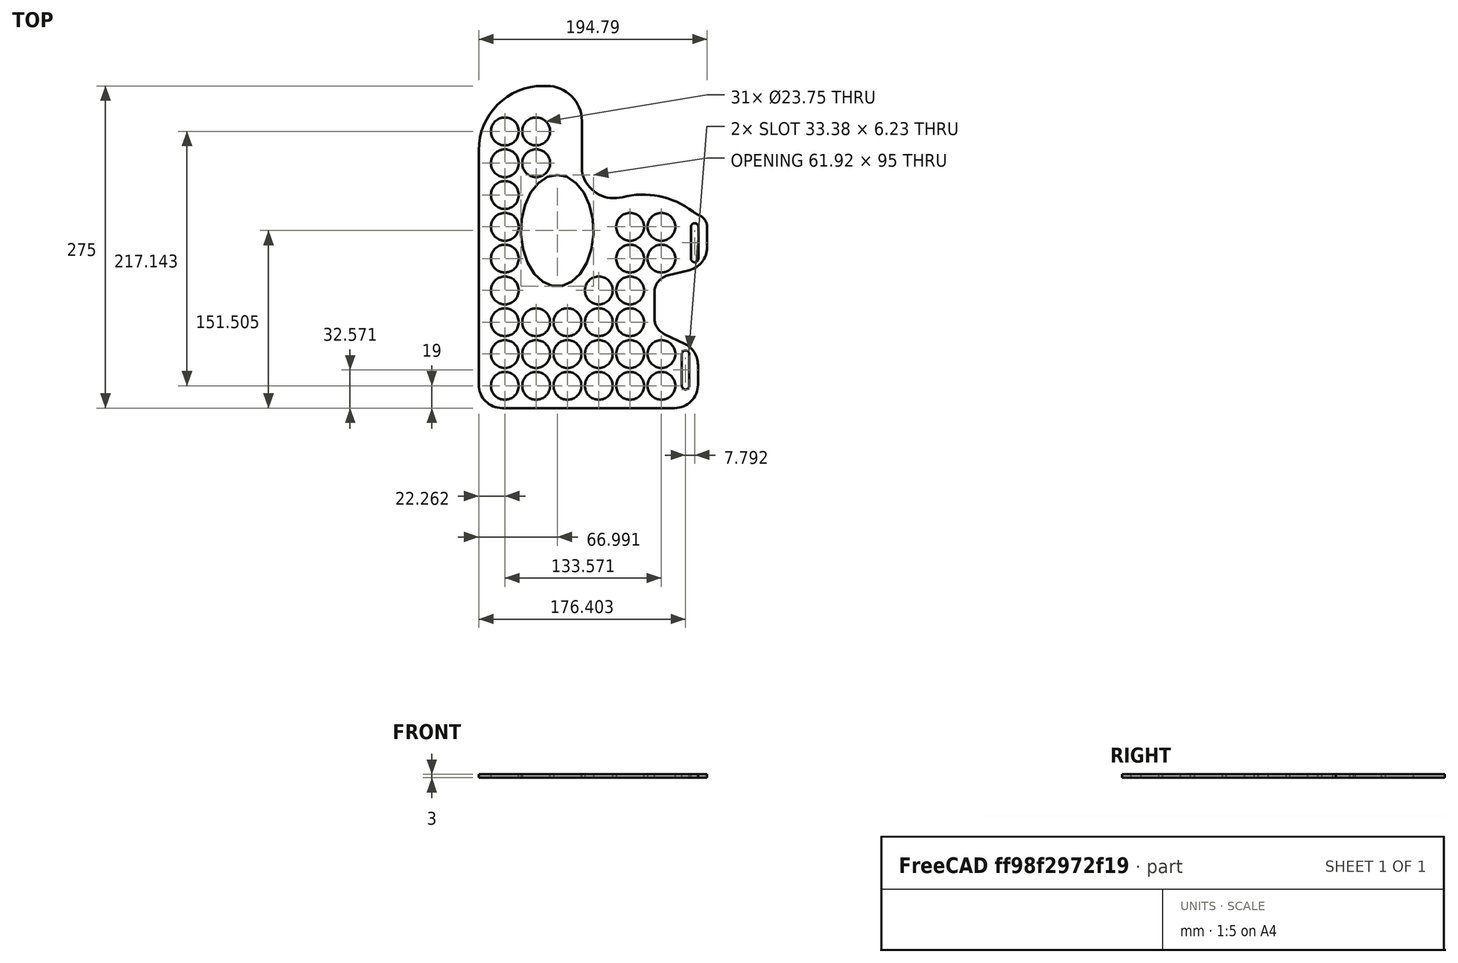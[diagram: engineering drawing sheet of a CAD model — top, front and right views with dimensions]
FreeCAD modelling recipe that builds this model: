
FCSTD DOCUMENT  (FreeCAD 0.18R4 (GitTag))
Label: ortese
License: All rights reserved
LicenseURL: http://en.wikipedia.org/wiki/All_rights_reserved
objects: Sketcher::SketchObject×1, PartDesign::Pad×1, PartDesign::Body×1
note: 4 computed .brp shape members not serialized (recipe doc carries the construction recipe); baked Part::Feature solids carry a one-line shape summary decoded from their .brp

FEATURE [Sketcher::SketchObject] Sketch
  MapMode = 5
  Support = -> [XY_Plane]
  expr: Constraints[176] = Sketch.Constraints.larguraOrtese / 30
  expr: Constraints[111] = Constraints.hFuros
  expr: Constraints[56] = Constraints.larguraOrtese / 3.12
  expr: Constraints[168] = Sketch.Constraints.larguraOrtese / 25
  expr: Constraints[147] = Sketch.Constraints.hFuros
  expr: Constraints[93] = Constraints.lFuros / 1.2
  expr: Constraints[39] = Constraints.larguraOrtese / 3.4
  expr: Constraints[153] = Sketch.Constraints.hFuros
  expr: Constraints[140] = Sketch.Constraints.hFuros
  expr: Constraints[21] = Constraints.alturaMao / 1.9
  expr: Constraints[51] = Constraints.larguraOrtese / 5.19
  expr: Constraints[28] = Constraints.alturaMao / 1.51
  expr: Constraints[144] = Sketch.Constraints.hFuros
  expr: Constraints[87] = Constraints.lFuros
  expr: Constraints[155] = Sketch.Constraints.hFuros
  expr: Constraints[63] = Constraints.alturaMao / 1.9
  expr: Constraints[167] = Sketch.Constraints.larguraOrtese / 30
  expr: Constraints.hFuro = Sketch.Constraints.alturaMao / 5
  expr: Constraints[45] = Constraints.larguraOrtese / 2.125
  expr: Constraints[13] = Constraints.larguraOrtese / 3.02
  expr: Constraints[145] = Sketch.Constraints.lFuros
  expr: Constraints[113] = Sketch.Constraints.lFuros
  expr: Constraints.hFuros = Sketch.Constraints.alturaMao / 3.5
  expr: Constraints[92] = Constraints.lFuros
  expr: Constraints.lFuros = Constraints.larguraOrtese / 7
  expr: Constraints[110] = Constraints.hFuros
  expr: Constraints[175] = Sketch.Constraints.larguraOrtese / 25
  expr: Constraints[120] = Sketch.Constraints.alturaMao / 8
  expr: Constraints[108] = Constraints.hFuros
  expr: Constraints[12] = Constraints.alturaMao
  expr: Constraints[46] = Constraints.alturaMao / 1.73
  expr: Constraints[88] = Constraints.lFuros
  expr: Constraints[60] = Constraints.larguraOrtese / 0.96
  expr: Constraints[86] = Constraints.lFuros
  expr: Constraints[29] = Constraints.larguraOrtese / 4.16
  expr: Constraints[50] = Constraints.alturaMao / 1.25
  sketch-geometry (66):
    g0: LineSegment StartX=-3.7e-15 StartY=0 StartZ=0 EndX=147 EndY=0 EndZ=0
    g1: LineSegment StartX=-20 StartY=20 StartZ=0 EndX=-20 EndY=220.005 EndZ=0
    g2: LineSegment StartX=35 StartY=275.005 StartZ=0 EndX=38 EndY=275.005 EndZ=0
    g3: LineSegment StartX=68 StartY=245.005 StartZ=0 EndX=68 EndY=204.345 EndZ=0
    g4: LineSegment StartX=174.792 StartY=154.889 StartZ=0 EndX=174.792 EndY=137.218 EndZ=0
    g5: LineSegment StartX=159.691 StartY=117.827 StartZ=0 EndX=141.165 EndY=113.147 EndZ=0
    g6: LineSegment StartX=129.84 StartY=98.6038 StartZ=0 EndX=129.84 EndY=76.6828 EndZ=0
    g7: LineSegment StartX=138.376 StartY=63.1469 StartZ=0 EndX=155.618 EndY=54.9133 EndZ=0
    g8: LineSegment StartX=167 StartY=36.8654 StartZ=0 EndX=167 EndY=20 EndZ=0
    g9: Ellipse CenterX=46.9911 CenterY=151.505 CenterZ=0 NormalX=0 NormalY=0 NormalZ=1 MajorRadius=47.5 MinorRadius=30.9603 AngleXU=1.5708
    g10: LineSegment [constr] StartX=46.9911 StartY=199.005 StartZ=0 EndX=46.9911 EndY=104.005 EndZ=0
    g11: LineSegment [constr] StartX=16.0308 StartY=151.505 StartZ=0 EndX=77.9514 EndY=151.505 EndZ=0
    g12: GeomPoint X=46.9911 Y=187.528 Z=0
    g13: GeomPoint X=46.9911 Y=115.481 Z=0
    g14: ArcOfCircle CenterX=144.84 CenterY=76.6828 CenterZ=0 NormalX=0 NormalY=0 NormalZ=1 AngleXU=0 Radius=15 StartAngle=3.14159 EndAngle=4.26688
    g15: ArcOfCircle CenterX=144.84 CenterY=98.6038 CenterZ=0 NormalX=0 NormalY=0 NormalZ=1 AngleXU=0 Radius=15 StartAngle=1.81826 EndAngle=3.14159
    g16: ArcOfCircle CenterX=154.792 CenterY=137.218 CenterZ=0 NormalX=0 NormalY=0 NormalZ=1 AngleXU=0 Radius=20 StartAngle=4.95986 EndAngle=6.28319
    g17: ArcOfCircle CenterX=147 CenterY=36.8654 CenterZ=0 NormalX=0 NormalY=0 NormalZ=1 AngleXU=0 Radius=20 StartAngle=0 EndAngle=1.12529
    g18: ArcOfCircle CenterX=164.792 CenterY=154.889 CenterZ=0 NormalX=0 NormalY=0 NormalZ=1 AngleXU=0 Radius=10 StartAngle=0 EndAngle=1.14527
    g19: ArcOfCircle CenterX=88 CenterY=204.345 CenterZ=0 NormalX=0 NormalY=0 NormalZ=1 AngleXU=0 Radius=20 StartAngle=3.14159 EndAngle=3.50529
    g20: ArcOfCircle CenterX=38 CenterY=245.005 CenterZ=0 NormalX=0 NormalY=0 NormalZ=1 AngleXU=0 Radius=30 StartAngle=0 EndAngle=1.5708
    g21: ArcOfCircle CenterX=35 CenterY=220.005 CenterZ=0 NormalX=0 NormalY=0 NormalZ=1 AngleXU=0 Radius=55 StartAngle=1.5708 EndAngle=3.14159
    g22: ArcOfCircle CenterX=0 CenterY=20 CenterZ=0 NormalX=0 NormalY=0 NormalZ=1 AngleXU=0 Radius=20 StartAngle=3.14159 EndAngle=4.71239
    g23: ArcOfCircle CenterX=147 CenterY=20 CenterZ=0 NormalX=0 NormalY=0 NormalZ=1 AngleXU=0 Radius=20 StartAngle=4.71239 EndAngle=6.28319
    g24: ArcOfCircle CenterX=120.011 CenterY=112.21 CenterZ=0 NormalX=0 NormalY=0 NormalZ=1 AngleXU=0 Radius=70 StartAngle=0.918247 EndAngle=1.82246
    g25: ArcOfCircle CenterX=95.5804 CenterY=207.23 CenterZ=0 NormalX=0 NormalY=0 NormalZ=1 AngleXU=0 Radius=28.1109 StartAngle=3.50529 EndAngle=4.96405
    g26: ArcOfCircle CenterX=182.516 CenterY=193.997 CenterZ=0 NormalX=0 NormalY=0 NormalZ=1 AngleXU=0 Radius=32.9373 StartAngle=4.05984 EndAngle=4.28686
    g27: Circle CenterX=2.2619 CenterY=46.1429 CenterZ=0 NormalX=0 NormalY=0 NormalZ=1 AngleXU=0 Radius=11.875
    g28: Circle CenterX=28.9762 CenterY=46.1429 CenterZ=0 NormalX=0 NormalY=0 NormalZ=1 AngleXU=0 Radius=11.875
    g29: Circle CenterX=55.6905 CenterY=46.1429 CenterZ=0 NormalX=0 NormalY=0 NormalZ=1 AngleXU=0 Radius=11.875
    g30: Circle CenterX=82.4048 CenterY=46.1429 CenterZ=0 NormalX=0 NormalY=0 NormalZ=1 AngleXU=0 Radius=11.875
    g31: Circle CenterX=109.119 CenterY=46.1429 CenterZ=0 NormalX=0 NormalY=0 NormalZ=1 AngleXU=0 Radius=11.875
    g32: Circle CenterX=2.2619 CenterY=19 CenterZ=0 NormalX=0 NormalY=0 NormalZ=1 AngleXU=0 Radius=11.875
    g33: Circle CenterX=28.9762 CenterY=19 CenterZ=0 NormalX=0 NormalY=0 NormalZ=1 AngleXU=0 Radius=11.875
    g34: Circle CenterX=55.6905 CenterY=19 CenterZ=0 NormalX=0 NormalY=0 NormalZ=1 AngleXU=0 Radius=11.875
    g35: Circle CenterX=82.4048 CenterY=19 CenterZ=0 NormalX=0 NormalY=0 NormalZ=1 AngleXU=0 Radius=11.875
    g36: Circle CenterX=109.119 CenterY=19 CenterZ=0 NormalX=0 NormalY=0 NormalZ=1 AngleXU=0 Radius=11.875
    g37: Circle CenterX=135.833 CenterY=46.1429 CenterZ=0 NormalX=0 NormalY=0 NormalZ=1 AngleXU=0 Radius=11.875
    g38: Circle CenterX=135.833 CenterY=19 CenterZ=0 NormalX=0 NormalY=0 NormalZ=1 AngleXU=0 Radius=11.875
    g39: Circle CenterX=2.2619 CenterY=73.2857 CenterZ=0 NormalX=0 NormalY=0 NormalZ=1 AngleXU=0 Radius=11.875
    g40: Circle CenterX=28.9762 CenterY=73.2857 CenterZ=0 NormalX=0 NormalY=0 NormalZ=1 AngleXU=0 Radius=11.875
    g41: Circle CenterX=55.6905 CenterY=73.2857 CenterZ=0 NormalX=0 NormalY=0 NormalZ=1 AngleXU=0 Radius=11.875
    g42: Circle CenterX=82.4048 CenterY=73.2857 CenterZ=0 NormalX=0 NormalY=0 NormalZ=1 AngleXU=0 Radius=11.875
    g43: Circle CenterX=109.119 CenterY=73.2857 CenterZ=0 NormalX=0 NormalY=0 NormalZ=1 AngleXU=0 Radius=11.875
    g44: Circle CenterX=2.2619 CenterY=100.429 CenterZ=0 NormalX=0 NormalY=0 NormalZ=1 AngleXU=0 Radius=11.875
    g45: Circle CenterX=109.119 CenterY=127.571 CenterZ=0 NormalX=0 NormalY=0 NormalZ=1 AngleXU=0 Radius=11.875
    g46: Circle CenterX=2.2619 CenterY=127.571 CenterZ=0 NormalX=0 NormalY=0 NormalZ=1 AngleXU=0 Radius=11.875
    g47: Circle CenterX=2.2619 CenterY=154.714 CenterZ=0 NormalX=0 NormalY=0 NormalZ=1 AngleXU=0 Radius=11.875
    g48: Circle CenterX=109.119 CenterY=154.714 CenterZ=0 NormalX=0 NormalY=0 NormalZ=1 AngleXU=0 Radius=11.875
    g49: Circle CenterX=135.833 CenterY=154.714 CenterZ=0 NormalX=0 NormalY=0 NormalZ=1 AngleXU=0 Radius=11.875
    g50: Circle CenterX=135.833 CenterY=127.571 CenterZ=0 NormalX=0 NormalY=0 NormalZ=1 AngleXU=0 Radius=11.875
    g51: Circle CenterX=82.4048 CenterY=100.429 CenterZ=0 NormalX=0 NormalY=0 NormalZ=1 AngleXU=0 Radius=11.875
    g52: Circle CenterX=109.119 CenterY=100.429 CenterZ=0 NormalX=0 NormalY=0 NormalZ=1 AngleXU=0 Radius=11.875
    g53: Circle CenterX=2.2619 CenterY=181.857 CenterZ=0 NormalX=0 NormalY=0 NormalZ=1 AngleXU=0 Radius=11.875
    g54: Circle CenterX=2.2619 CenterY=209 CenterZ=0 NormalX=0 NormalY=0 NormalZ=1 AngleXU=0 Radius=11.875
    g55: Circle CenterX=28.9762 CenterY=209 CenterZ=0 NormalX=0 NormalY=0 NormalZ=1 AngleXU=0 Radius=11.875
    g56: Circle CenterX=2.2619 CenterY=236.143 CenterZ=0 NormalX=0 NormalY=0 NormalZ=1 AngleXU=0 Radius=11.875
    g57: Circle CenterX=28.9762 CenterY=236.143 CenterZ=0 NormalX=0 NormalY=0 NormalZ=1 AngleXU=0 Radius=11.875
    g58: ArcOfCircle CenterX=156.403 CenterY=46.1429 CenterZ=0 NormalX=0 NormalY=0 NormalZ=1 AngleXU=0 Radius=3.11667 StartAngle=-9e-16 EndAngle=3.14159
    g59: ArcOfCircle CenterX=156.403 CenterY=19 CenterZ=0 NormalX=0 NormalY=0 NormalZ=1 AngleXU=0 Radius=3.11667 StartAngle=3.14159 EndAngle=6.28319
    g60: LineSegment StartX=153.287 StartY=46.1429 StartZ=0 EndX=153.287 EndY=19 EndZ=0
    g61: LineSegment StartX=159.52 StartY=46.1429 StartZ=0 EndX=159.52 EndY=19 EndZ=0
    g62: ArcOfCircle CenterX=164.195 CenterY=154.714 CenterZ=0 NormalX=0 NormalY=0 NormalZ=1 AngleXU=0 Radius=3.11667 StartAngle=1e-15 EndAngle=3.14159
    g63: ArcOfCircle CenterX=164.195 CenterY=127.571 CenterZ=0 NormalX=0 NormalY=0 NormalZ=1 AngleXU=0 Radius=3.11667 StartAngle=3.14159 EndAngle=6.28319
    g64: LineSegment StartX=161.078 StartY=154.714 StartZ=0 EndX=161.078 EndY=127.571 EndZ=0
    g65: LineSegment StartX=167.312 StartY=154.714 StartZ=0 EndX=167.312 EndY=127.571 EndZ=0
  constraints (176):
    c: Horizontal(g2)
    c: Vertical(g8)
    c: Vertical(g1)
    c: Vertical(g3)
    c: Vertical(g6)
    c: Equal(g5,g7)
    c: Vertical(g4)
    c: PointOnObject(g-1,g0)
    c: InternalAlignment(g10-g13 -> g9) x4
    c: DistanceY(g10,g10) = 95
    c: DistanceX(g11,g11) = 61.9205
    c: Vertical(g10)
    c: Tangent(g6,g14) = -1.5708
    c: Tangent(g7,g14) = -1.5708
    c: DistanceX(g6,g14) = 15
    c: Tangent(g6,g15) = -1.5708
    c: Tangent(g5,g15) = -1.5708
    c: DistanceX(g6,g15) = 15
    c: DistanceY(g7,g5) = 50
    c: Tangent(g5,g16) = 1.5708
    c: Tangent(g4,g16) = 1.5708
    c: DistanceX(g16,g4) = 20
    c: Tangent(g7,g17) = 1.5708
    c: Tangent(g8,g17) = 1.5708
    c: DistanceX(g17,g8) = 20
    c: DistanceY(g7,g5) = 62.9139
    c: DistanceX(g6,g4) = 44.9519
    c: Tangent(g4,g18) = 1.5708
    c: DistanceX(g18,g4) = 10
    c: Tangent(g3,g19) = -1.5708
    c: DistanceX(g3,g19) = 20
    c: Tangent(g2,g20) = 1.5708
    c: Tangent(g3,g20) = 1.5708
    c: Tangent(g2,g21) = 1.5708
    c: Tangent(g1,g21) = 1.5708
    c: DistanceX(g20,g3) = 30
    c: DistanceX(g1,g21) = 55
    c: Tangent(g1,g22) = 1.5708
    c: Tangent(g0,g22) = -1.5708
    c: Tangent(g0,g23) = -1.5708
    c: Tangent(g8,g23) = 1.5708
    c: DistanceX(g23,g8) = 20
    c: DistanceX(g1,g3) = 88
    c: DistanceY(g0,g7) = 54.9133
    c: DistanceX(g1,g8) = 187  'larguraOrtese'
    c: Radius(g24) = 70
    c: PointOnObject(g0,g-2)
    c: DistanceY(g10,g2) = 76
    c: DistanceX(g1,g11) = 36.0308
    c: Tangent(g19,g25) = -1.5708
    c: Tangent(g24,g25) = 1.5708
    c: Tangent(g18,g26) = 1.5708
    c: Tangent(g24,g26) = 1.5708
    c: DistanceX(g24,g24) = 59.9359
    c: DistanceY(g24,g2) = 95  'alturaMao'
    c: DistanceY(g19,g25) = 10
    c: DistanceX(g25,g24) = 7
    c: DistanceX(g1,g4) = 194.792
    c: DistanceY(g18,g26) = 30
    c: DistanceX(g24,g26) = 20
    c: DistanceY(g5,g24) = 50
    c: Horizontal(g0)
    c: Horizontal(g32,g33)
    c: Horizontal(g33,g34)
    c: Horizontal(g34,g35)
    c: Horizontal(g35,g36)
    c: Horizontal(g27,g28)
    c: Horizontal(g28,g29)
    c: Horizontal(g29,g30)
    c: Horizontal(g30,g31)
    c: Vertical(g32,g27)
    c: Vertical(g33,g28)
    c: Vertical(g34,g29)
    c: Equal(g28,g27)
    c: Equal(g27,g32)
    c: Equal(g32,g33)
    c: Equal(g30,g29)
    c: Equal(g29,g34)
    c: Equal(g34,g35)
    c: Equal(g35,g31)
    c: Equal(g31,g36)
    c: Vertical(g36,g31)
    c: DistanceX(g35,g36) = 26.7143  'lFuros'
    c: DistanceX(g34,g35) = 26.7143
    c: DistanceX(g33,g34) = 26.7143
    c: DistanceX(g32,g33) = 26.7143
    c: Horizontal(g38,g35)
    c: Horizontal(g37,g29)
    c: Vertical(g37,g38)
    c: DistanceX(g36,g38) = 26.7143
    c: DistanceX(g1,g32) = 22.2619
    c: DistanceY(g0,g32) = 19  'hFuro'
    c: DistanceY(g32,g27) = 27.1429  'hFuros'
    c: Horizontal(g39,g40)
    c: Horizontal(g40,g41)
    c: Horizontal(g41,g42)
    c: Horizontal(g42,g43)
    c: Equal(g40,g39)
    c: Equal(g42,g41)
    c: Vertical(g39,g27)
    c: Vertical(g33,g40)
    c: Vertical(g41,g34)
    c: Vertical(g30,g42)
    c: Vertical(g42,g35)
    c: DistanceX(g1,g22) = 20
    c: DistanceY(g30,g42) = 27.1429
    c: Vertical(g44,g39)
    c: DistanceY(g39,g44) = 27.1429
    c: DistanceY(g46,g47) = 27.1429
    c: Horizontal(g46,g45)
    c: DistanceX(g45,g50) = 26.7143
    c: Equal(g48,g49)
    c: Equal(g49,g50)
    c: Equal(g50,g45)
    c: Equal(g47,g46)
    c: Equal(g46,g44)
    c: Equal(g44,g39)
    c: Radius(g32) = 11.875
    c: Equal(g33,g34)
    c: Equal(g41,g29)
    c: Vertical(g46,g44)
    c: Horizontal(g50,g45)
    c: Horizontal(g47,g48)
    c: Horizontal(g48,g49)
    c: Vertical(g47,g46)
    c: Vertical(g49,g50)
    c: Horizontal(g44,g51)
    c: Horizontal(g51,g52)
    c: Vertical(g51,g42)
    c: Vertical(g52,g43)
    c: Vertical(g43,g36)
    c: Equal(g51,g52)
    c: Equal(g52,g43)
    c: Equal(g43,g37)
    c: Equal(g37,g38)
    c: Equal(g38,g35)
    c: Equal(g40,g32)
    c: DistanceY(g44,g46) = 27.1429
    c: Vertical(g48,g52)
    c: Vertical(g52,g45)
    c: Equal(g45,g32)
    c: DistanceY(g55,g57) = 27.1429
    c: DistanceX(g54,g57) = 26.7143
    c: Vertical(g57,g55)
    c: DistanceY(g54,g56) = 27.1429
    c: Equal(g53,g32)
    c: Equal(g56,g32)
    c: Equal(g55,g57)
    c: Equal(g57,g54)
    c: Equal(g54,g32)
    c: DistanceY(g53,g54) = 27.1429
    c: Horizontal(g56,g57)
    c: DistanceY(g47,g53) = 27.1429
    c: Vertical(g54,g53)
    c: Vertical(g53,g56)
    c: Vertical(g56,g47)
    c: Tangent(g58,g61) = 1.5708
    c: Tangent(g58,g60) = -1.5708
    c: Tangent(g60,g59) = -1.5708
    c: Tangent(g61,g59) = 1.5708
    c: Vertical(g60)
    c: Equal(g58,g59)
    c: Horizontal(g58,g37)
    c: Horizontal(g59,g33)
    c: DistanceX(g58,g58) = 6.23333
    c: DistanceX(g58,g8) = 7.48
    c: Tangent(g62,g65) = 1.5708
    c: Tangent(g62,g64) = -1.5708
    c: Tangent(g64,g63) = -1.5708
    c: Tangent(g65,g63) = 1.5708
    c: Vertical(g64)
    c: Equal(g62,g63)
    c: DistanceX(g62,g4) = 7.48
    c: DistanceX(g62,g62) = 6.23333
    c: Horizontal(g49,g62)
    c: Horizontal(g50,g63)
FEATURE [PartDesign::Pad] Pad
  Length = 3
  Length2 = 100
  Profile = -> Sketch
  Type = 0
FEATURE [PartDesign::Body] Body
  Group = -> [Sketch,Pad]
  Origin = -> Origin
  Tip = -> Pad
